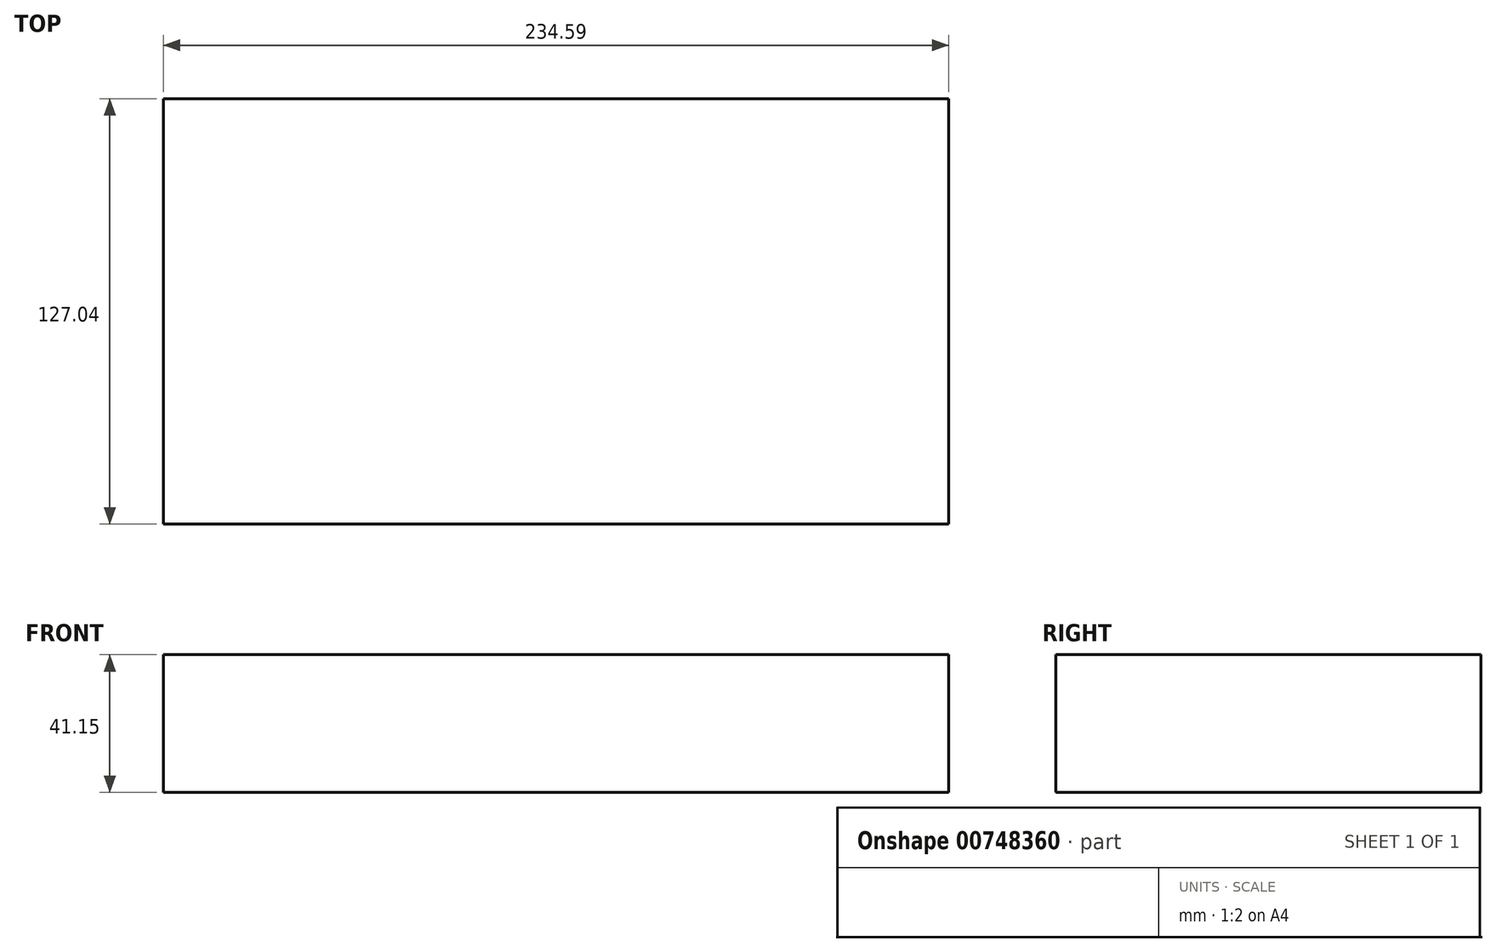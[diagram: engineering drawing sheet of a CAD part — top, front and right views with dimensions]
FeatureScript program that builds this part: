
annotation { "Feature Type Name" : "Feature", "Feature Type Description" : "" }
export const myFeature = defineFeature(function(context is Context, id is Id, definition is map)
    precondition{}
    {
        {
            var Q0;
            Q0=qCreatedBy(makeId("Top.planeOp"),FACE);
            var sketch = newSketch(context, id + "F0", { "sketchPlane" : qUnion([Q0])});
            skLineSegment(sketch, "E0.bottom", {"start": v(-119.62, 53.27) * mm, "end": v(114.97, 53.27) * mm});
            skLineSegment(sketch, "E0.top", {"start": v(-119.62, -73.77) * mm, "end": v(114.97, -73.77) * mm});
            skLineSegment(sketch, "E0.left", {"start": v(-119.62, 53.27) * mm, "end": v(-119.62, -73.77) * mm});
            skLineSegment(sketch, "E0.right", {"start": v(114.97, 53.27) * mm, "end": v(114.97, -73.77) * mm});
            skSolve(sketch);
        }
        {
            var Q0;
            Q0 = qSketchRegion(id + "F0", true);
            extrude(context, id + "F1", {"entities" : qUnion([Q0]), "depth" : 41.15 * mm, "offsetDistance" : 25.4 * mm});
        }
    });
